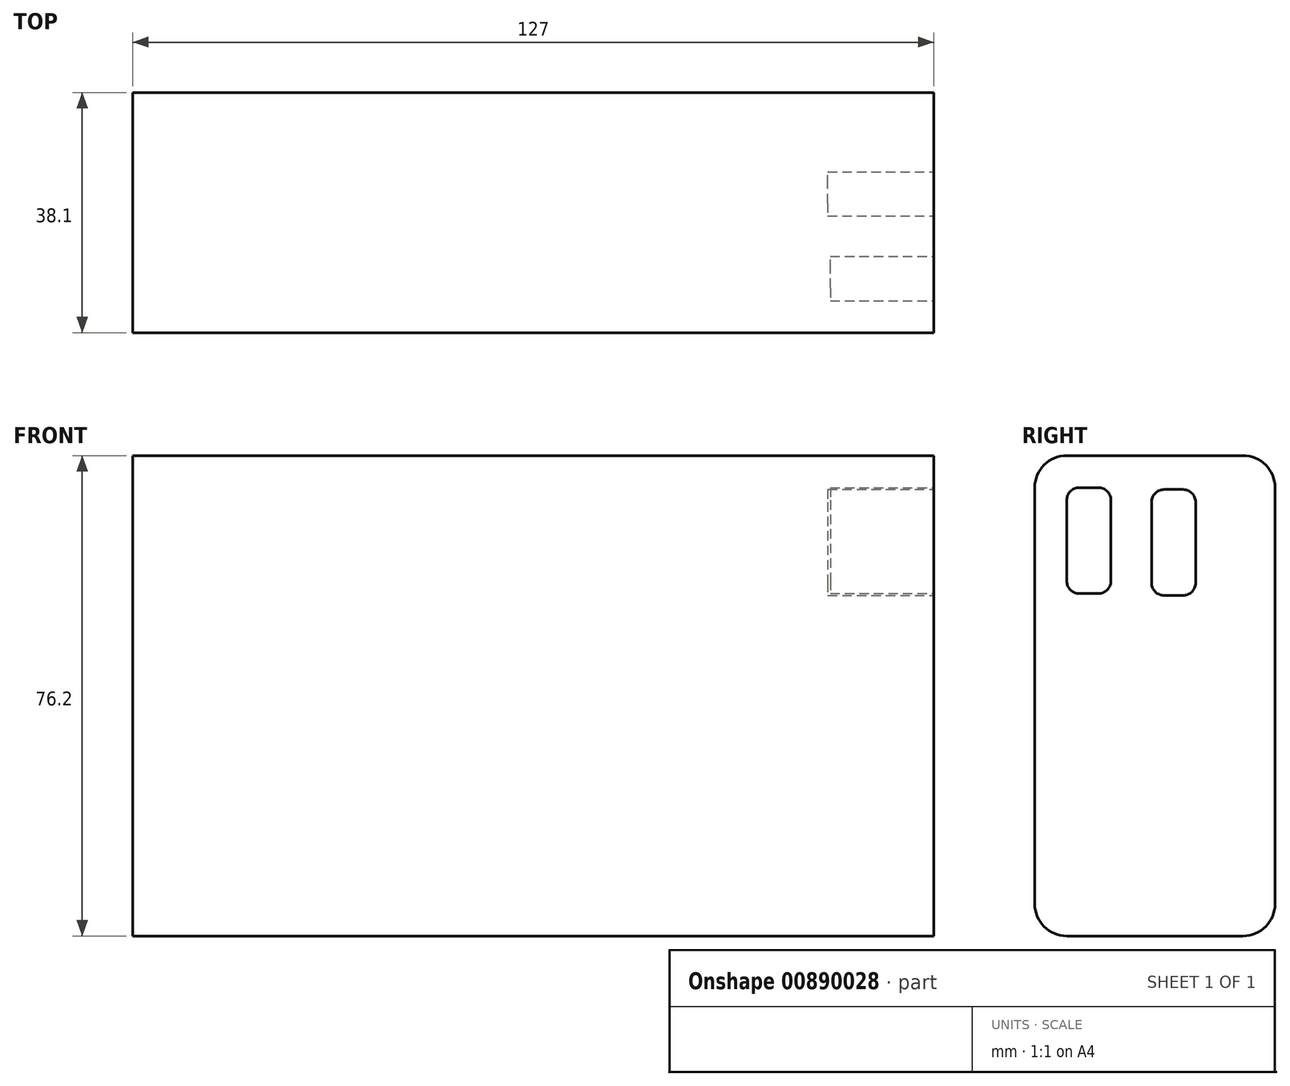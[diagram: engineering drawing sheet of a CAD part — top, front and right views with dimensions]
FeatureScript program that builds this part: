
annotation { "Feature Type Name" : "Feature", "Feature Type Description" : "" }
export const myFeature = defineFeature(function(context is Context, id is Id, definition is map)
    precondition{}
    {
        {
            var Q0;
            Q0=qCreatedBy(makeId("Front.planeOp"),FACE);
            var sketch = newSketch(context, id + "F0", { "sketchPlane" : qUnion([Q0])});
            skLineSegment(sketch, "E0.bottom", {"start": v(63.5, -38.1) * mm, "end": v(-63.5, -38.1) * mm});
            skLineSegment(sketch, "E0.top", {"start": v(63.5, 38.1) * mm, "end": v(-63.5, 38.1) * mm});
            skLineSegment(sketch, "E0.left", {"start": v(63.5, -38.1) * mm, "end": v(63.5, 38.1) * mm});
            skLineSegment(sketch, "E0.right", {"start": v(-63.5, -38.1) * mm, "end": v(-63.5, 38.1) * mm});
            skPoint(sketch, "E0.middle", {"position": v(0, 0) * mm});
            skSolve(sketch);
        }
        {
            var Q0;
            Q0=makeQuery(id+"F0.imprint","IMPRINT",FACE,{"disambiguationData":[TD([[makeQuery(id+"F0.imprint","IMPRINT",EDGE,{"derivedFrom":sQuery(id+"F0.wireOp",EDGE,"E0.bottom")}),-1.0]])]});
            extrude(context, id + "F1", {"entities" : qUnion([Q0]), "depth" : 38.1 * mm, "offsetDistance" : 25.4 * mm});
        }
        {
            var Q0;
            Q0=makeQuery(id+"F1.opExtrude","CAP_EDGE",EDGE,{"disambiguationData":[OSD([sQuery(id+"F0.wireOp",EDGE,"E0.top")])],"isStart":false});
            var Q1;
            Q1=makeQuery(id+"F1.opExtrude","CAP_EDGE",EDGE,{"disambiguationData":[OSD([sQuery(id+"F0.wireOp",EDGE,"E0.top")])],"isStart":true});
            var Q2;
            Q2=makeQuery(id+"F1.opExtrude","CAP_EDGE",EDGE,{"disambiguationData":[OSD([sQuery(id+"F0.wireOp",EDGE,"E0.bottom")])],"isStart":false});
            var Q3;
            Q3=makeQuery(id+"F1.opExtrude","CAP_EDGE",EDGE,{"disambiguationData":[OSD([sQuery(id+"F0.wireOp",EDGE,"E0.bottom")])],"isStart":true});
            fillet(context, id + "F2", {"entities" : qUnion([Q0, Q1, Q2, Q3]), "radius" : 5.08 * mm, "tangentPropagation" : true, "allowEdgeOverflow" : false});
        }
        {
            var Q0;
            Q0=makeQuery(id+"F1.opExtrude","SWEPT_FACE",FACE,{"disambiguationData":[OSD([sQuery(id+"F0.wireOp",EDGE,"E0.left")])]});
            var sketch = newSketch(context, id + "F3", { "sketchPlane" : qUnion([Q0])});
            skLineSegment(sketch, "E1.bottom", {"start": v(-31.02, 33.02) * mm, "end": v(-28.02, 33.02) * mm});
            skLineSegment(sketch, "E1.top", {"start": v(-31.02, 16.22) * mm, "end": v(-28.02, 16.22) * mm});
            skLineSegment(sketch, "E1.left", {"start": v(-33.02, 31.02) * mm, "end": v(-33.02, 18.22) * mm});
            skLineSegment(sketch, "E1.right", {"start": v(-26.02, 31.02) * mm, "end": v(-26.02, 18.22) * mm});
            skPoint(sketch, "E2.visualSharp", {"position": v(-33.02, 33.02) * mm});
            skArc(sketch, "E2.filletArc", {"start": v(-31.02, 33.02) * mm, "mid": v(-32.43, 32.43) * mm, "end": v(-33.02, 31.02) * mm});
            skPoint(sketch, "E3.visualSharp", {"position": v(-33.02, 16.22) * mm});
            skArc(sketch, "E3.filletArc", {"start": v(-33.02, 18.22) * mm, "mid": v(-32.43, 16.8) * mm, "end": v(-31.02, 16.22) * mm});
            skPoint(sketch, "E4.visualSharp", {"position": v(-26.02, 33.02) * mm});
            skArc(sketch, "E4.filletArc", {"start": v(-26.02, 31.02) * mm, "mid": v(-26.6, 32.43) * mm, "end": v(-28.02, 33.02) * mm});
            skPoint(sketch, "E5.visualSharp", {"position": v(-26.02, 16.22) * mm});
            skArc(sketch, "E5.filletArc", {"start": v(-28.02, 16.22) * mm, "mid": v(-26.6, 16.8) * mm, "end": v(-26.02, 18.22) * mm});
            skSolve(sketch);
        }
        {
            var Q0;
            Q0=makeQuery(id+"F3.imprint","IMPRINT",FACE,{"disambiguationData":[TD([[makeQuery(id+"F3.imprint","IMPRINT",EDGE,{"derivedFrom":sQuery(id+"F3.wireOp",EDGE,"E1.bottom")}),-1.0]])]});
            extrude(context, id + "F4", {"entities" : qUnion([Q0]), "operationType" : NewBodyOperationType.REMOVE, "oppositeDirection" : true, "depth" : 16.4 * mm, "offsetDistance" : 25.4 * mm});
        }
        {
            var Q0;
            Q0=makeQuery(id+"F3.imprint","IMPRINT",FACE,{"disambiguationData":[TD([[makeQuery(id+"F3.imprint","IMPRINT",EDGE,{"derivedFrom":sQuery(id+"F3.wireOp",EDGE,"E1.bottom")}),1.0]])]});
            var sketch = newSketch(context, id + "F5", { "sketchPlane" : qUnion([Q0])});
            skLineSegment(sketch, "E6.bottom", {"start": v(-17.58, 32.72) * mm, "end": v(-14.58, 32.72) * mm});
            skLineSegment(sketch, "E6.top", {"start": v(-17.58, 15.92) * mm, "end": v(-14.58, 15.92) * mm});
            skLineSegment(sketch, "E6.left", {"start": v(-19.58, 30.72) * mm, "end": v(-19.58, 17.92) * mm});
            skLineSegment(sketch, "E6.right", {"start": v(-12.58, 30.72) * mm, "end": v(-12.58, 17.92) * mm});
            skPoint(sketch, "E7.visualSharp", {"position": v(-19.58, 32.72) * mm});
            skArc(sketch, "E7.filletArc", {"start": v(-17.58, 32.72) * mm, "mid": v(-19, 32.13) * mm, "end": v(-19.58, 30.72) * mm});
            skPoint(sketch, "E8.visualSharp", {"position": v(-19.58, 15.92) * mm});
            skArc(sketch, "E8.filletArc", {"start": v(-19.58, 17.92) * mm, "mid": v(-19, 16.5) * mm, "end": v(-17.58, 15.92) * mm});
            skPoint(sketch, "E9.visualSharp", {"position": v(-12.58, 32.72) * mm});
            skArc(sketch, "E9.filletArc", {"start": v(-12.58, 30.72) * mm, "mid": v(-13.17, 32.13) * mm, "end": v(-14.58, 32.72) * mm});
            skPoint(sketch, "E10.visualSharp", {"position": v(-12.58, 15.92) * mm});
            skArc(sketch, "E10.filletArc", {"start": v(-14.58, 15.92) * mm, "mid": v(-13.17, 16.5) * mm, "end": v(-12.58, 17.92) * mm});
            skSolve(sketch);
        }
        {
            var Q0;
            Q0=makeQuery(id+"F5.imprint","IMPRINT",FACE,{"disambiguationData":[TD([[makeQuery(id+"F5.imprint","IMPRINT",EDGE,{"derivedFrom":sQuery(id+"F5.wireOp",EDGE,"E6.bottom")}),-1.0]])]});
            extrude(context, id + "F6", {"entities" : qUnion([Q0]), "operationType" : NewBodyOperationType.REMOVE, "oppositeDirection" : true, "depth" : 16.8 * mm, "offsetDistance" : 25.4 * mm});
        }
    });
